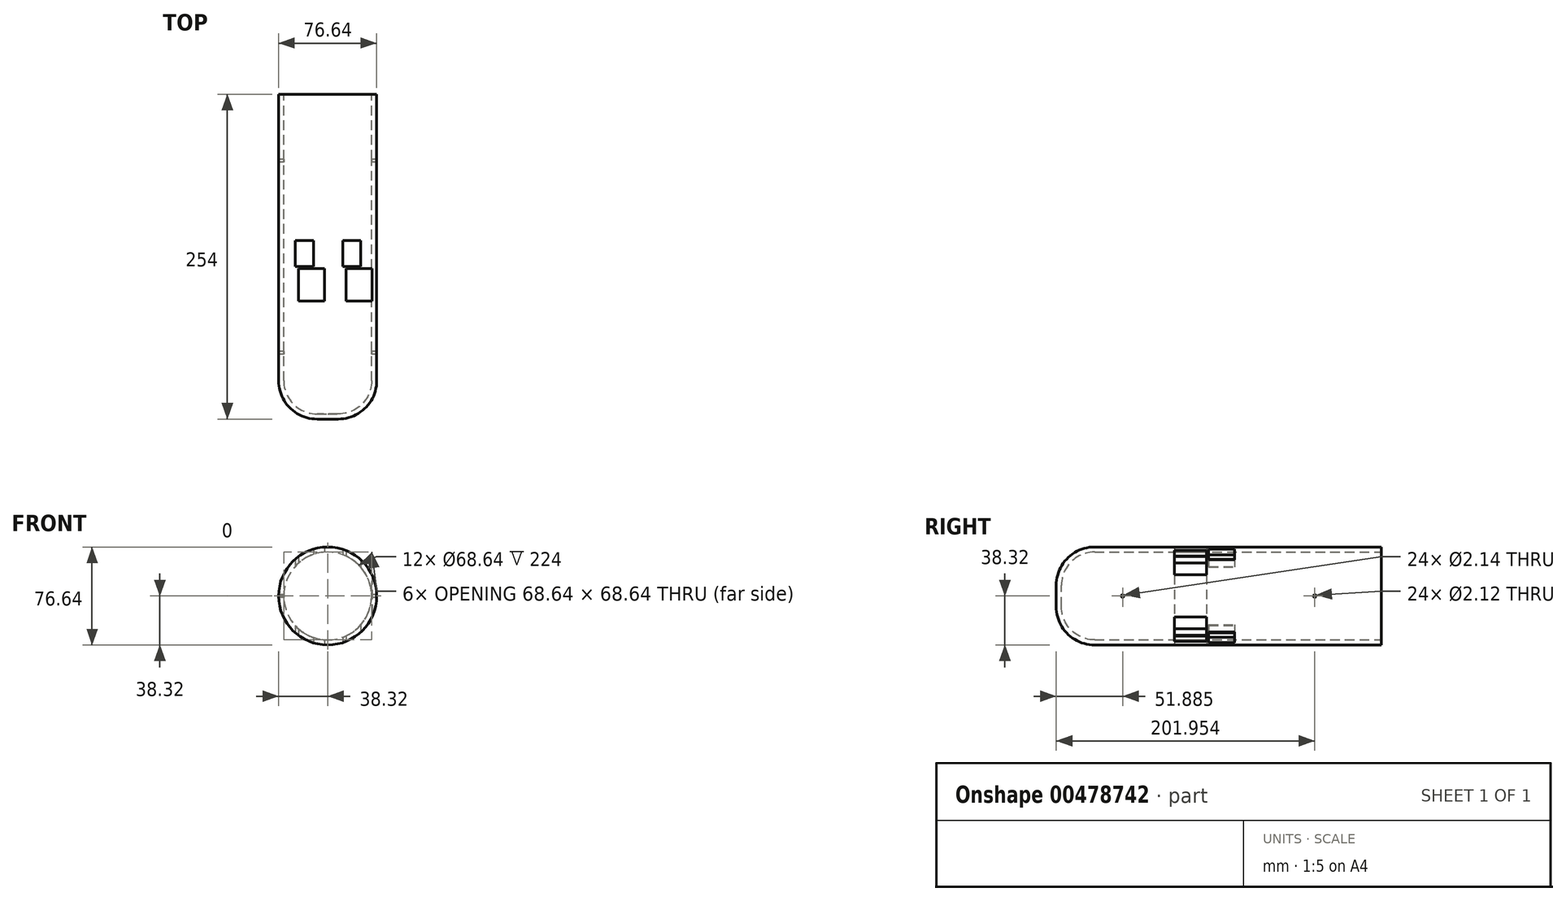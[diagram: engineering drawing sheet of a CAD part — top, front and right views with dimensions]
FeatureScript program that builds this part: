
annotation { "Feature Type Name" : "Feature", "Feature Type Description" : "" }
export const myFeature = defineFeature(function(context is Context, id is Id, definition is map)
    precondition{}
    {
        {
            var Q0;
            Q0=qCreatedBy(makeId("Front.planeOp"),FACE);
            var sketch = newSketch(context, id + "F0", { "sketchPlane" : qUnion([Q0])});
            skCircle(sketch, "E0", {"center": v(0, 0) * mm, "radius": 38.32 * mm});
            skSolve(sketch);
        }
        {
            var Q0;
            Q0=makeQuery(id+"F0.imprint","IMPRINT",FACE,{"disambiguationData":[TD([[makeQuery(id+"F0.imprint","IMPRINT",EDGE,{"derivedFrom":sQuery(id+"F0.wireOp",EDGE,"E0")}),1.0]])]});
            extrude(context, id + "F1", {"entities" : qUnion([Q0]), "endBound" : BoundingType.SYMMETRIC, "depth" : 254 * mm});
        }
        {
            var Q0;
            Q0=makeQuery(id+"F1.opExtrude","CAP_EDGE",EDGE,{"disambiguationData":[OSD([sQuery(id+"F0.wireOp",EDGE,"E0")])],"isStart":false});
            fillet(context, id + "F2", {"entities" : qUnion([Q0]), "radius" : 30 * mm, "tangentPropagation" : true, "allowEdgeOverflow" : false});
        }
        {
            var Q0;
            Q0=makeQuery(id+"F1.opExtrude","CAP_FACE",FACE,{"disambiguationData":[OSD([sQuery(id+"F0.wireOp",EDGE,"E0")])],"isStart":true});
            shell(context, id + "F3", {"entities" : qUnion([Q0]), "thickness" : 4 * mm});
        }
        {
            var Q0;
            Q0=qCreatedBy(makeId("Right.planeOp"),FACE);
            var sketch = newSketch(context, id + "F4", { "sketchPlane" : qUnion([Q0])});
            skCircle(sketch, "E1", {"center": v(-75.12, 0) * mm, "radius": 1.07 * mm});
            skCircle(sketch, "E2", {"center": v(74.95, 0) * mm, "radius": 1.06 * mm});
            skSolve(sketch);
        }
        {
            var Q0;
            Q0=makeQuery(id+"F4.imprint","IMPRINT",FACE,{"disambiguationData":[TD([[makeQuery(id+"F4.imprint","IMPRINT",EDGE,{"derivedFrom":sQuery(id+"F4.wireOp",EDGE,"E1")}),1.0]])]});
            extrude(context, id + "F5", {"entities" : qUnion([Q0]), "operationType" : NewBodyOperationType.REMOVE, "endBound" : BoundingType.SYMMETRIC, "depth" : 100 * mm});
        }
        {
            var Q0;
            Q0=makeQuery(id+"F4.imprint","IMPRINT",FACE,{"disambiguationData":[TD([[makeQuery(id+"F4.imprint","IMPRINT",EDGE,{"derivedFrom":sQuery(id+"F4.wireOp",EDGE,"E2")}),1.0]])]});
            var Q1;
            Q1=sQuery(id+"F4.wireOp",EDGE,"E2");
            extrude(context, id + "F6", {"entities" : qUnion([Q0]), "operationType" : NewBodyOperationType.REMOVE, "surfaceEntities" : qUnion([Q1]), "endBound" : BoundingType.SYMMETRIC, "depth" : 100 * mm});
        }
        {
            var Q0;
            Q0=qCreatedBy(makeId("Top.planeOp"),FACE);
            var sketch = newSketch(context, id + "F7", { "sketchPlane" : qUnion([Q0])});
            skLineSegment(sketch, "E3.bottom", {"start": v(-11.18, 12.45) * mm, "end": v(-25.4, 12.45) * mm});
            skLineSegment(sketch, "E3.top", {"start": v(-11.18, -7.87) * mm, "end": v(-25.4, -7.87) * mm});
            skLineSegment(sketch, "E3.left", {"start": v(-11.18, 12.45) * mm, "end": v(-11.18, -7.87) * mm});
            skLineSegment(sketch, "E3.right", {"start": v(-25.4, 12.45) * mm, "end": v(-25.4, -7.87) * mm});
            skLineSegment(sketch, "E4.bottom", {"start": v(11.68, 12.45) * mm, "end": v(25.9, 12.45) * mm});
            skLineSegment(sketch, "E4.top", {"start": v(11.68, -7.87) * mm, "end": v(25.9, -7.87) * mm});
            skLineSegment(sketch, "E4.left", {"start": v(11.68, 12.45) * mm, "end": v(11.68, -7.87) * mm});
            skLineSegment(sketch, "E4.right", {"start": v(25.9, 12.45) * mm, "end": v(25.9, -7.87) * mm});
            skLineSegment(sketch, "E5.bottom", {"start": v(-2.52, -34.7) * mm, "end": v(-22.71, -34.7) * mm});
            skLineSegment(sketch, "E5.top", {"start": v(-2.52, -9.24) * mm, "end": v(-22.71, -9.24) * mm});
            skLineSegment(sketch, "E5.left", {"start": v(-2.52, -34.7) * mm, "end": v(-2.52, -9.24) * mm});
            skLineSegment(sketch, "E5.right", {"start": v(-22.71, -34.7) * mm, "end": v(-22.71, -9.24) * mm});
            skPoint(sketch, "E5.middle", {"position": v(-12.62, -21.97) * mm});
            skLineSegment(sketch, "E6.bottom", {"start": v(14.3, -9.48) * mm, "end": v(34.6, -9.48) * mm});
            skLineSegment(sketch, "E6.top", {"start": v(14.3, -34.73) * mm, "end": v(34.6, -34.73) * mm});
            skLineSegment(sketch, "E6.left", {"start": v(14.3, -9.48) * mm, "end": v(14.3, -34.73) * mm});
            skLineSegment(sketch, "E6.right", {"start": v(34.6, -9.48) * mm, "end": v(34.6, -34.73) * mm});
            skPoint(sketch, "E6.middle", {"position": v(24.45, -22.1) * mm});
            skSolve(sketch);
        }
        {
            var Q0;
            Q0=makeQuery(id+"F7.imprint","IMPRINT",FACE,{"disambiguationData":[TD([[makeQuery(id+"F7.imprint","IMPRINT",EDGE,{"derivedFrom":sQuery(id+"F7.wireOp",EDGE,"E4.bottom")}),-1.0]])]});
            var Q1;
            Q1=makeQuery(id+"F7.imprint","IMPRINT",FACE,{"disambiguationData":[TD([[makeQuery(id+"F7.imprint","IMPRINT",EDGE,{"derivedFrom":sQuery(id+"F7.wireOp",EDGE,"E3.bottom")}),1.0]])]});
            extrude(context, id + "F8", {"entities" : qUnion([Q0, Q1]), "operationType" : NewBodyOperationType.REMOVE, "endBound" : BoundingType.SYMMETRIC, "depth" : 100 * mm});
        }
        {
            var Q0;
            Q0=makeQuery(id+"F7.imprint","IMPRINT",FACE,{"disambiguationData":[TD([[makeQuery(id+"F7.imprint","IMPRINT",EDGE,{"derivedFrom":sQuery(id+"F7.wireOp",EDGE,"E6.bottom")}),-1.0]])]});
            var Q1;
            Q1=makeQuery(id+"F7.imprint","IMPRINT",FACE,{"disambiguationData":[TD([[makeQuery(id+"F7.imprint","IMPRINT",EDGE,{"derivedFrom":sQuery(id+"F7.wireOp",EDGE,"E5.bottom")}),-1.0]])]});
            extrude(context, id + "F9", {"entities" : qUnion([Q0, Q1]), "operationType" : NewBodyOperationType.REMOVE, "endBound" : BoundingType.SYMMETRIC, "depth" : 100 * mm});
        }
    });
